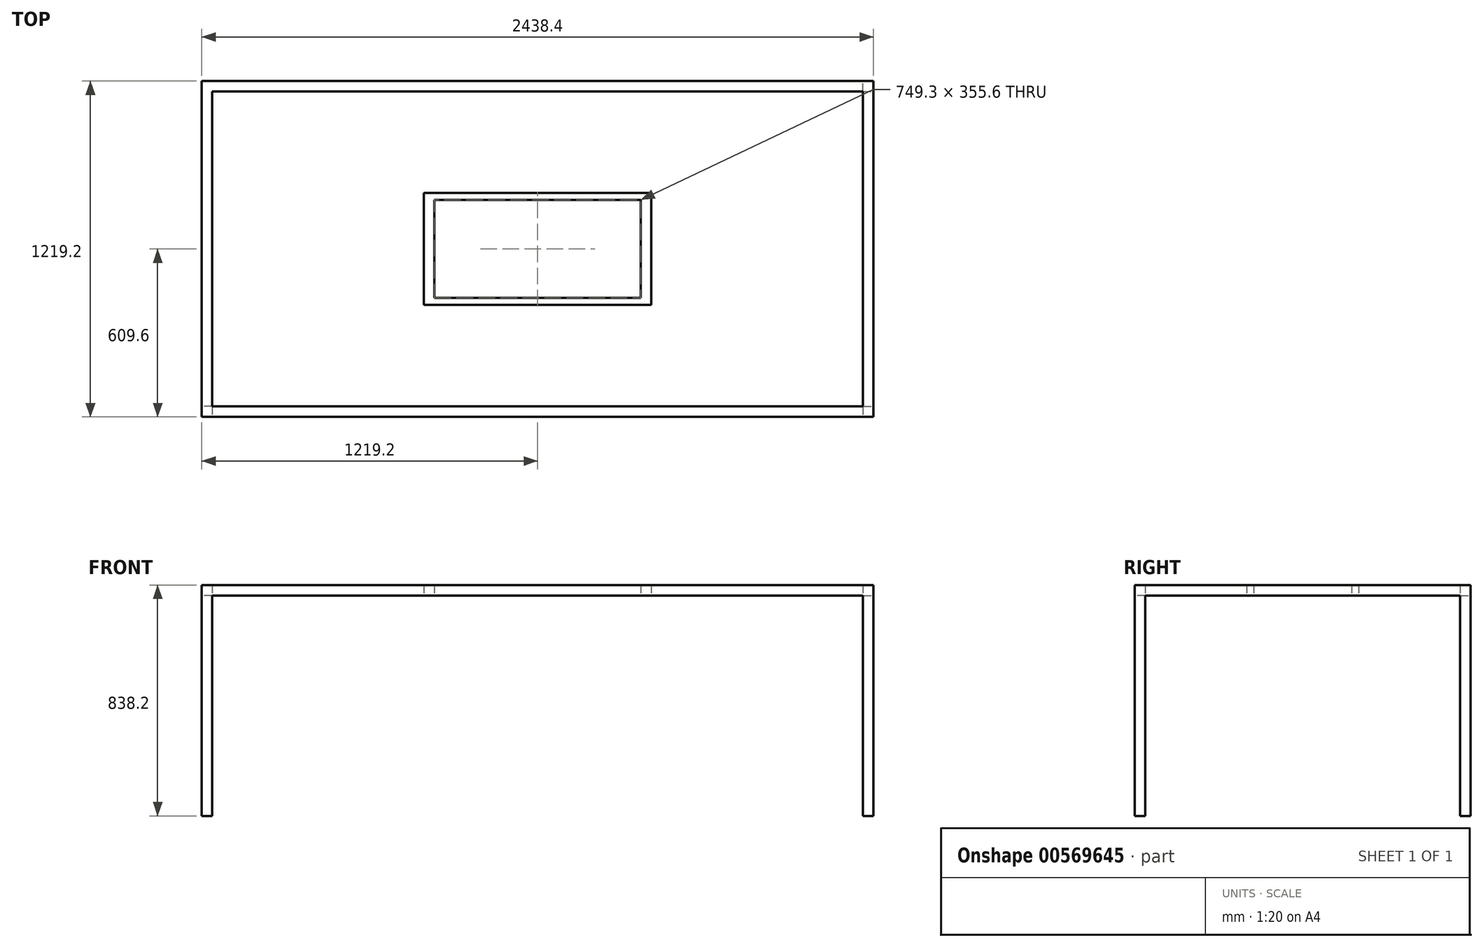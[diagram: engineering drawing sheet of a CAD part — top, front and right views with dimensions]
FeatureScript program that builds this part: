
annotation { "Feature Type Name" : "Feature", "Feature Type Description" : "" }
export const myFeature = defineFeature(function(context is Context, id is Id, definition is map)
    precondition{}
    {
        {
            var Q0;
            Q0=qCreatedBy(makeId("Top.planeOp"),FACE);
            var sketch = newSketch(context, id + "F0", { "sketchPlane" : qUnion([Q0])});
            skLineSegment(sketch, "E0.bottom", {"start": v(1219.2, 609.6) * mm, "end": v(-1219.2, 609.6) * mm});
            skLineSegment(sketch, "E0.top", {"start": v(1219.2, -609.6) * mm, "end": v(-1219.2, -609.6) * mm});
            skLineSegment(sketch, "E0.left", {"start": v(1219.2, 609.6) * mm, "end": v(1219.2, -609.6) * mm});
            skLineSegment(sketch, "E0.right", {"start": v(-1219.2, 609.6) * mm, "end": v(-1219.2, -609.6) * mm});
            skPoint(sketch, "E0.middle", {"position": v(0, 0) * mm});
            skLineSegment(sketch, "E1.0", {"start": v(1181.1, 571.5) * mm, "end": v(-1181.1, 571.5) * mm});
            skLineSegment(sketch, "E1.1", {"start": v(1181.1, 571.5) * mm, "end": v(1181.1, -571.5) * mm});
            skLineSegment(sketch, "E1.2", {"start": v(1181.1, -571.5) * mm, "end": v(-1181.1, -571.5) * mm});
            skLineSegment(sketch, "E1.3", {"start": v(-1181.1, 571.5) * mm, "end": v(-1181.1, -571.5) * mm});
            skLineSegment(sketch, "E2.bottom", {"start": v(-1219.2, 609.6) * mm, "end": v(-1181.1, 609.6) * mm});
            skLineSegment(sketch, "E2.top", {"start": v(-1219.2, 571.5) * mm, "end": v(-1181.1, 571.5) * mm});
            skLineSegment(sketch, "E2.left", {"start": v(-1219.2, 609.6) * mm, "end": v(-1219.2, 571.5) * mm});
            skLineSegment(sketch, "E2.right", {"start": v(-1181.1, 609.6) * mm, "end": v(-1181.1, 571.5) * mm});
            skLineSegment(sketch, "E3.bottom", {"start": v(-1181.1, -571.5) * mm, "end": v(-1219.2, -571.5) * mm});
            skLineSegment(sketch, "E3.top", {"start": v(-1181.1, -609.6) * mm, "end": v(-1219.2, -609.6) * mm});
            skLineSegment(sketch, "E3.left", {"start": v(-1181.1, -571.5) * mm, "end": v(-1181.1, -609.6) * mm});
            skLineSegment(sketch, "E3.right", {"start": v(-1219.2, -571.5) * mm, "end": v(-1219.2, -609.6) * mm});
            skLineSegment(sketch, "E4.bottom", {"start": v(1181.1, -571.5) * mm, "end": v(1219.2, -571.5) * mm});
            skLineSegment(sketch, "E4.top", {"start": v(1181.1, -609.6) * mm, "end": v(1219.2, -609.6) * mm});
            skLineSegment(sketch, "E4.left", {"start": v(1181.1, -571.5) * mm, "end": v(1181.1, -609.6) * mm});
            skLineSegment(sketch, "E4.right", {"start": v(1219.2, -571.5) * mm, "end": v(1219.2, -609.6) * mm});
            skLineSegment(sketch, "E5.bottom", {"start": v(1181.1, 571.5) * mm, "end": v(1219.2, 571.5) * mm});
            skLineSegment(sketch, "E5.top", {"start": v(1181.1, 609.6) * mm, "end": v(1219.2, 609.6) * mm});
            skLineSegment(sketch, "E5.left", {"start": v(1181.1, 571.5) * mm, "end": v(1181.1, 609.6) * mm});
            skLineSegment(sketch, "E5.right", {"start": v(1219.2, 571.5) * mm, "end": v(1219.2, 609.6) * mm});
            skLineSegment(sketch, "E6", {"start": v(0, -609.6) * mm, "end": v(0, -571.5) * mm, "construction": true});
            skLineSegment(sketch, "E7", {"start": v(0, 609.6) * mm, "end": v(0, 571.5) * mm, "construction": true});
            skLineSegment(sketch, "E8.bottom", {"start": v(19.05, 609.6) * mm, "end": v(-19.05, 609.6) * mm});
            skLineSegment(sketch, "E8.top", {"start": v(19.05, 571.5) * mm, "end": v(-19.05, 571.5) * mm});
            skLineSegment(sketch, "E8.left", {"start": v(19.05, 609.6) * mm, "end": v(19.05, 571.5) * mm});
            skLineSegment(sketch, "E8.right", {"start": v(-19.05, 609.6) * mm, "end": v(-19.05, 571.5) * mm});
            skPoint(sketch, "E8.middle", {"position": v(0, 590.55) * mm});
            skLineSegment(sketch, "E9.bottom", {"start": v(19.05, -571.5) * mm, "end": v(-19.05, -571.5) * mm});
            skLineSegment(sketch, "E9.top", {"start": v(19.05, -609.6) * mm, "end": v(-19.05, -609.6) * mm});
            skLineSegment(sketch, "E9.left", {"start": v(19.05, -571.5) * mm, "end": v(19.05, -609.6) * mm});
            skLineSegment(sketch, "E9.right", {"start": v(-19.05, -571.5) * mm, "end": v(-19.05, -609.6) * mm});
            skPoint(sketch, "E9.middle", {"position": v(0, -590.55) * mm});
            skLineSegment(sketch, "E10", {"start": v(-1181.1, 0) * mm, "end": v(-393.7, 0) * mm});
            skPoint(sketch, "E10.endSnap0", {"position": v(-1181.1, 0) * mm});
            skLineSegment(sketch, "E11", {"start": v(-393.7, 0) * mm, "end": v(393.7, 0) * mm});
            skLineSegment(sketch, "E12", {"start": v(393.7, 0) * mm, "end": v(1181.1, 0) * mm});
            skLineSegment(sketch, "E13.bottom", {"start": v(-374.65, -571.5) * mm, "end": v(-412.75, -571.5) * mm});
            skLineSegment(sketch, "E13.top", {"start": v(-374.65, 571.5) * mm, "end": v(-412.75, 571.5) * mm});
            skLineSegment(sketch, "E13.left", {"start": v(-374.65, -571.5) * mm, "end": v(-374.65, 571.5) * mm});
            skLineSegment(sketch, "E13.right", {"start": v(-412.75, -571.5) * mm, "end": v(-412.75, 571.5) * mm});
            skPoint(sketch, "E13.middle", {"position": v(-393.7, 0) * mm});
            skLineSegment(sketch, "E14.bottom", {"start": v(412.75, 571.5) * mm, "end": v(374.65, 571.5) * mm});
            skLineSegment(sketch, "E14.top", {"start": v(412.75, -571.5) * mm, "end": v(374.65, -571.5) * mm});
            skLineSegment(sketch, "E14.left", {"start": v(412.75, 571.5) * mm, "end": v(412.75, -571.5) * mm});
            skLineSegment(sketch, "E14.right", {"start": v(374.65, 571.5) * mm, "end": v(374.65, -571.5) * mm});
            skPoint(sketch, "E14.middle", {"position": v(393.7, 0) * mm});
            skLineSegment(sketch, "E15", {"start": v(0, 571.5) * mm, "end": v(0, 190.5) * mm});
            skLineSegment(sketch, "E16", {"start": v(0, 190.5) * mm, "end": v(0, -190.5) * mm});
            skLineSegment(sketch, "E17.bottom", {"start": v(-1181.1, 203.2) * mm, "end": v(1181.1, 203.2) * mm});
            skLineSegment(sketch, "E17.top", {"start": v(-1181.1, 177.8) * mm, "end": v(1181.1, 177.8) * mm});
            skLineSegment(sketch, "E17.left", {"start": v(-1181.1, 203.2) * mm, "end": v(-1181.1, 177.8) * mm});
            skLineSegment(sketch, "E17.right", {"start": v(1181.1, 203.2) * mm, "end": v(1181.1, 177.8) * mm});
            skPoint(sketch, "E17.middle", {"position": v(0, 190.5) * mm});
            skLineSegment(sketch, "E18.left", {"start": v(-1181.1, -190.5) * mm, "end": v(-1181.1, -190.5) * mm});
            skLineSegment(sketch, "E18.right", {"start": v(1181.1, -190.5) * mm, "end": v(1181.1, -190.5) * mm});
            skPoint(sketch, "E18.middle", {"position": v(0, -190.5) * mm});
            skLineSegment(sketch, "E19.bottom", {"start": v(-1181.1, -203.2) * mm, "end": v(1181.1, -203.2) * mm});
            skLineSegment(sketch, "E19.top", {"start": v(-1181.1, -177.8) * mm, "end": v(1181.1, -177.8) * mm});
            skLineSegment(sketch, "E19.left", {"start": v(-1181.1, -203.2) * mm, "end": v(-1181.1, -177.8) * mm});
            skLineSegment(sketch, "E19.right", {"start": v(1181.1, -203.2) * mm, "end": v(1181.1, -177.8) * mm});
            skSolve(sketch);
        }
        {
            var Q0;
            Q0 = qSketchRegion(id + "F0", true);
            var Q1;
            {var subQ1=sQuery(id+"F0.wireOp",EDGE,"E13.top");Q1=makeQuery(id+"F0.imprint","IMPRINT",FACE,{"disambiguationData":[TD([[makeQuery(id+"F0.imprint","IMPRINT",EDGE,{"derivedFrom":subQ1}),1.0]])]});}
            var Q2;
            {var subQ1=sQuery(id+"F0.wireOp",EDGE,"E13.bottom");Q2=makeQuery(id+"F0.imprint","IMPRINT",FACE,{"disambiguationData":[TD([[makeQuery(id+"F0.imprint","IMPRINT",EDGE,{"derivedFrom":subQ1}),-1.0]])]});}
            var Q3;
            {var subQ0=sQuery(id+"F0.wireOp",EDGE,"E14.bottom");Q3=makeQuery(id+"F0.imprint","IMPRINT",FACE,{"disambiguationData":[TD([[makeQuery(id+"F0.imprint","IMPRINT",EDGE,{"derivedFrom":subQ0}),1.0]])]});}
            var Q4;
            {var subQ1=sQuery(id+"F0.wireOp",EDGE,"E14.top");Q4=makeQuery(id+"F0.imprint","IMPRINT",FACE,{"disambiguationData":[TD([[makeQuery(id+"F0.imprint","IMPRINT",EDGE,{"derivedFrom":subQ1}),-1.0]])]});}
            var Q5;
            {var subQ1=sQuery(id+"F0.wireOp",EDGE,"E11");var subQ6=sQuery(id+"F0.wireOp",EDGE,"E12");var subQ9=makeQuery(id+"F0.imprint","INTERSECT",VERTEX,{"derivedFrom":[subQ1,subQ6]});Q5=makeQuery(id+"F0.imprint","IMPRINT",FACE,{"disambiguationData":[TD([[makeQuery(id+"F0.imprint","IMPRINT",EDGE,{"disambiguationData":[TD([[subQ9,1.0]])],"derivedFrom":subQ1}),-1.0]])]});}
            var Q6;
            {var subQ1=sQuery(id+"F0.wireOp",EDGE,"E11");var subQ6=sQuery(id+"F0.wireOp",EDGE,"E12");var subQ9=makeQuery(id+"F0.imprint","INTERSECT",VERTEX,{"derivedFrom":[subQ1,subQ6]});Q6=makeQuery(id+"F0.imprint","IMPRINT",FACE,{"disambiguationData":[TD([[makeQuery(id+"F0.imprint","IMPRINT",EDGE,{"disambiguationData":[TD([[subQ9,1.0]])],"derivedFrom":subQ1}),1.0]])]});}
            var Q7;
            {var subQ0=sQuery(id+"F0.wireOp",EDGE,"E19.top");var subQ1=sQuery(id+"F0.wireOp",EDGE,"E14.left");var subQ2=makeQuery(id+"F0.imprint","INTERSECT",VERTEX,{"derivedFrom":[subQ1,subQ0]});Q7=makeQuery(id+"F0.imprint","IMPRINT",FACE,{"disambiguationData":[TD([[makeQuery(id+"F0.imprint","IMPRINT",EDGE,{"disambiguationData":[TD([[subQ2,-1.0]])],"derivedFrom":subQ1}),-1.0]])]});}
            var Q8;
            {var subQ0=sQuery(id+"F0.wireOp",EDGE,"E17.bottom");var subQ1=sQuery(id+"F0.wireOp",EDGE,"E14.left");var subQ2=makeQuery(id+"F0.imprint","INTERSECT",VERTEX,{"derivedFrom":[subQ1,subQ0]});Q8=makeQuery(id+"F0.imprint","IMPRINT",FACE,{"disambiguationData":[TD([[makeQuery(id+"F0.imprint","IMPRINT",EDGE,{"disambiguationData":[TD([[subQ2,-1.0]])],"derivedFrom":subQ1}),-1.0]])]});}
            var Q9;
            {var subQ0=sQuery(id+"F0.wireOp",EDGE,"E19.bottom");var subQ1=sQuery(id+"F0.wireOp",EDGE,"E13.left");var subQ2=makeQuery(id+"F0.imprint","INTERSECT",VERTEX,{"derivedFrom":[subQ1,subQ0]});Q9=makeQuery(id+"F0.imprint","IMPRINT",FACE,{"disambiguationData":[TD([[makeQuery(id+"F0.imprint","IMPRINT",EDGE,{"disambiguationData":[TD([[subQ2,-1.0]])],"derivedFrom":subQ1}),1.0]])]});}
            var Q10;
            {var subQ1=sQuery(id+"F0.wireOp",EDGE,"E10");var subQ6=sQuery(id+"F0.wireOp",EDGE,"E11");var subQ9=makeQuery(id+"F0.imprint","INTERSECT",VERTEX,{"derivedFrom":[subQ1,subQ6]});Q10=makeQuery(id+"F0.imprint","IMPRINT",FACE,{"disambiguationData":[TD([[makeQuery(id+"F0.imprint","IMPRINT",EDGE,{"disambiguationData":[TD([[subQ9,1.0]])],"derivedFrom":subQ1}),-1.0]])]});}
            var Q11;
            {var subQ1=sQuery(id+"F0.wireOp",EDGE,"E10");var subQ6=sQuery(id+"F0.wireOp",EDGE,"E11");var subQ9=makeQuery(id+"F0.imprint","INTERSECT",VERTEX,{"derivedFrom":[subQ1,subQ6]});Q11=makeQuery(id+"F0.imprint","IMPRINT",FACE,{"disambiguationData":[TD([[makeQuery(id+"F0.imprint","IMPRINT",EDGE,{"disambiguationData":[TD([[subQ9,1.0]])],"derivedFrom":subQ1}),1.0]])]});}
            var Q12;
            {var subQ0=sQuery(id+"F0.wireOp",EDGE,"E17.top");var subQ1=sQuery(id+"F0.wireOp",EDGE,"E13.left");var subQ2=makeQuery(id+"F0.imprint","INTERSECT",VERTEX,{"derivedFrom":[subQ1,subQ0]});Q12=makeQuery(id+"F0.imprint","IMPRINT",FACE,{"disambiguationData":[TD([[makeQuery(id+"F0.imprint","IMPRINT",EDGE,{"disambiguationData":[TD([[subQ2,-1.0]])],"derivedFrom":subQ1}),1.0]])]});}
            extrude(context, id + "F1", {"entities" : qUnion([Q0, Q1, Q2, Q3, Q4, Q5, Q6, Q7, Q8, Q9, Q10, Q11, Q12]), "depth" : 38.1 * mm, "offsetDistance" : 25.4 * mm});
        }
        {
            var Q0;
            Q0=makeQuery(id+"F0.imprint","IMPRINT",FACE,{"disambiguationData":[TD([[makeQuery(id+"F0.imprint","IMPRINT",EDGE,{"derivedFrom":sQuery(id+"F0.wireOp",EDGE,"E5.bottom")}),1.0]])]});
            var Q1;
            Q1=makeQuery(id+"F0.imprint","IMPRINT",FACE,{"disambiguationData":[TD([[makeQuery(id+"F0.imprint","IMPRINT",EDGE,{"derivedFrom":sQuery(id+"F0.wireOp",EDGE,"E4.bottom")}),-1.0]])]});
            var Q2;
            Q2=makeQuery(id+"F0.imprint","IMPRINT",FACE,{"disambiguationData":[TD([[makeQuery(id+"F0.imprint","IMPRINT",EDGE,{"derivedFrom":sQuery(id+"F0.wireOp",EDGE,"E9.bottom")}),1.0]])]});
            var Q3;
            Q3=makeQuery(id+"F0.imprint","IMPRINT",FACE,{"disambiguationData":[TD([[makeQuery(id+"F0.imprint","IMPRINT",EDGE,{"derivedFrom":sQuery(id+"F0.wireOp",EDGE,"E8.bottom")}),1.0]])]});
            var Q4;
            Q4=makeQuery(id+"F0.imprint","IMPRINT",FACE,{"disambiguationData":[TD([[makeQuery(id+"F0.imprint","IMPRINT",EDGE,{"derivedFrom":sQuery(id+"F0.wireOp",EDGE,"E2.bottom")}),-1.0]])]});
            var Q5;
            Q5=makeQuery(id+"F0.imprint","IMPRINT",FACE,{"disambiguationData":[TD([[makeQuery(id+"F0.imprint","IMPRINT",EDGE,{"derivedFrom":sQuery(id+"F0.wireOp",EDGE,"E3.bottom")}),1.0]])]});
            extrude(context, id + "F2", {"entities" : qUnion([Q0, Q1, Q2, Q3, Q4, Q5]), "operationType" : NewBodyOperationType.ADD, "oppositeDirection" : true, "depth" : 800.1 * mm, "offsetDistance" : 25.4 * mm});
        }
        {
            var Q0;
            {var subQ2=sQuery(id+"F0.wireOp",EDGE,"E13.left");var subQ4=sQuery(id+"F0.wireOp",EDGE,"E19.bottom");var subQ5=makeQuery(id+"F0.imprint","INTERSECT",VERTEX,{"derivedFrom":[subQ2,subQ4]});Q0=makeQuery(id+"F0.imprint","IMPRINT",FACE,{"disambiguationData":[TD([[makeQuery(id+"F0.imprint","IMPRINT",EDGE,{"disambiguationData":[TD([[subQ5,-1.0]])],"derivedFrom":subQ2}),-1.0]])]});}
            var Q1;
            {var subQ0=sQuery(id+"F0.wireOp",EDGE,"E17.bottom");var subQ1=sQuery(id+"F0.wireOp",EDGE,"E14.right");var subQ2=makeQuery(id+"F0.imprint","INTERSECT",VERTEX,{"derivedFrom":[subQ1,subQ0]});Q1=makeQuery(id+"F0.imprint","IMPRINT",FACE,{"disambiguationData":[TD([[makeQuery(id+"F0.imprint","IMPRINT",EDGE,{"disambiguationData":[TD([[subQ2,-1.0]])],"derivedFrom":subQ1}),-1.0]])]});}
            var Q2;
            {var subQ5=sQuery(id+"F0.wireOp",EDGE,"E17.left");Q2=makeQuery(id+"F0.imprint","IMPRINT",FACE,{"disambiguationData":[TD([[makeQuery(id+"F0.imprint","IMPRINT",EDGE,{"derivedFrom":subQ5}),1.0]])]});}
            var Q3;
            {var subQ1=sQuery(id+"F0.wireOp",EDGE,"E13.left");var subQ7=sQuery(id+"F0.wireOp",EDGE,"E17.top");var subQ9=makeQuery(id+"F0.imprint","INTERSECT",VERTEX,{"derivedFrom":[subQ1,subQ7]});Q3=makeQuery(id+"F0.imprint","IMPRINT",FACE,{"disambiguationData":[TD([[makeQuery(id+"F0.imprint","IMPRINT",EDGE,{"disambiguationData":[TD([[subQ9,-1.0]])],"derivedFrom":subQ1}),-1.0]])]});}
            var Q4;
            {var subQ5=sQuery(id+"F0.wireOp",EDGE,"E19.left");Q4=makeQuery(id+"F0.imprint","IMPRINT",FACE,{"disambiguationData":[TD([[makeQuery(id+"F0.imprint","IMPRINT",EDGE,{"derivedFrom":subQ5}),-1.0]])]});}
            var Q5;
            {var subQ5=sQuery(id+"F0.wireOp",EDGE,"E19.right");Q5=makeQuery(id+"F0.imprint","IMPRINT",FACE,{"disambiguationData":[TD([[makeQuery(id+"F0.imprint","IMPRINT",EDGE,{"derivedFrom":subQ5}),1.0]])]});}
            var Q6;
            {var subQ5=sQuery(id+"F0.wireOp",EDGE,"E17.right");Q6=makeQuery(id+"F0.imprint","IMPRINT",FACE,{"disambiguationData":[TD([[makeQuery(id+"F0.imprint","IMPRINT",EDGE,{"derivedFrom":subQ5}),-1.0]])]});}
            extrude(context, id + "F3", {"entities" : qUnion([Q0, Q1, Q2, Q3, Q4, Q5, Q6]), "operationType" : NewBodyOperationType.ADD, "depth" : 38.1 * mm, "offsetDistance" : 25.4 * mm});
        }
    });
